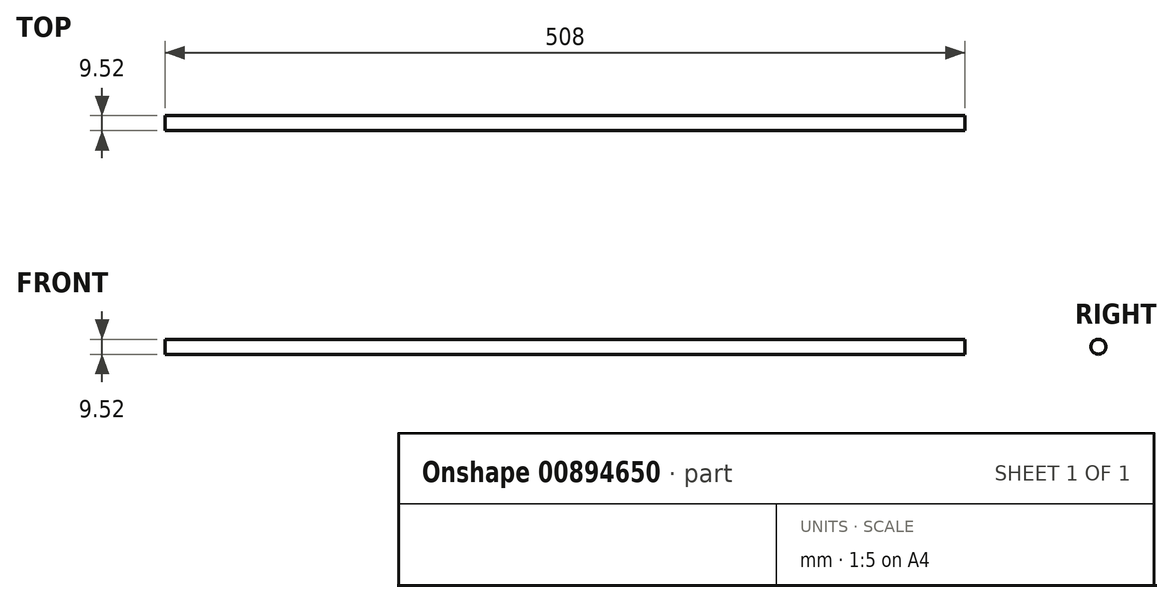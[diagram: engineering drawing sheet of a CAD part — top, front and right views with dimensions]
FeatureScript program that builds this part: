
annotation { "Feature Type Name" : "Feature", "Feature Type Description" : "" }
export const myFeature = defineFeature(function(context is Context, id is Id, definition is map)
    precondition{}
    {
        {
            var Q0;
            Q0=qCreatedBy(makeId("Right.planeOp"),FACE);
            var sketch = newSketch(context, id + "F0", { "sketchPlane" : qUnion([Q0])});
            skCircle(sketch, "E0", {"center": v(0, 0) * mm, "radius": 4.76 * mm});
            skSolve(sketch);
        }
        {
            var Q0;
            Q0=qSketchRegion(id+"F0",true);
            extrude(context, id + "F1", {"entities" : qUnion([Q0]), "endBound" : BoundingType.SYMMETRIC, "depth" : 508 * mm, "offsetDistance" : 25.4 * mm});
        }
    });
